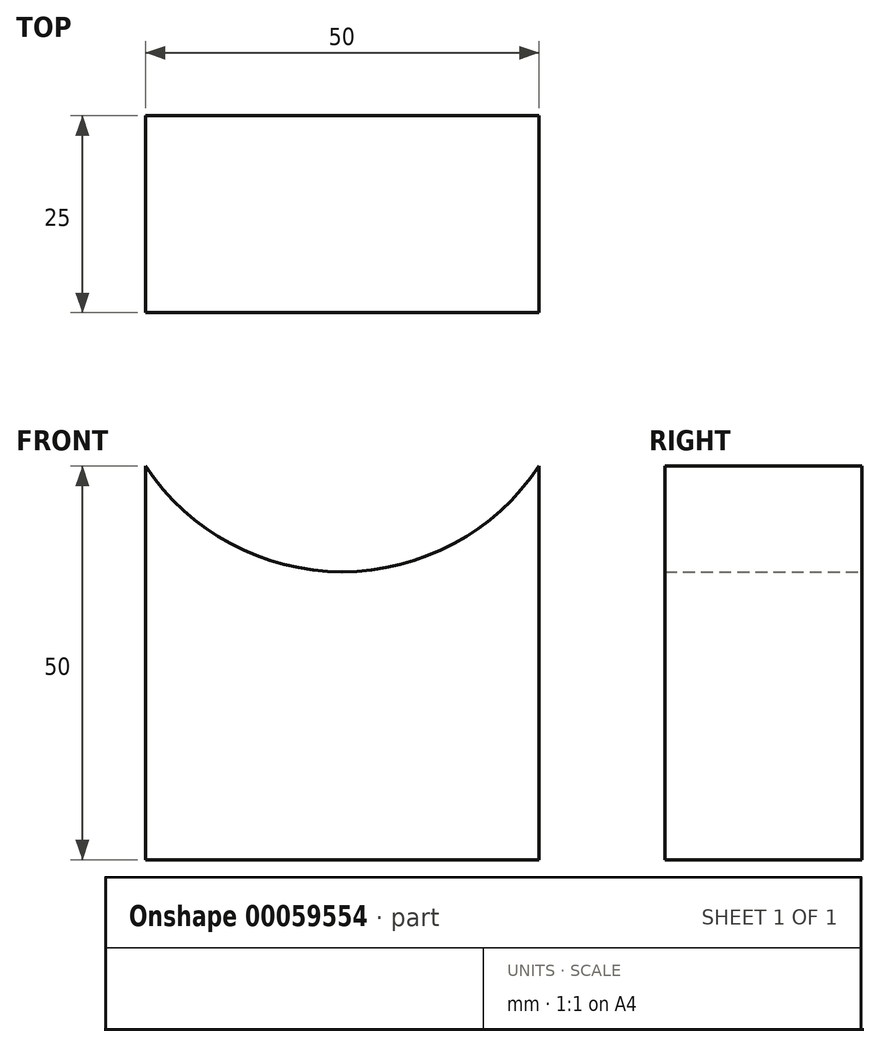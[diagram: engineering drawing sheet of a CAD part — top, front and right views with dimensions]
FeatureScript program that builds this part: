
annotation { "Feature Type Name" : "Feature", "Feature Type Description" : "" }
export const myFeature = defineFeature(function(context is Context, id is Id, definition is map)
    precondition{}
    {
        {
            var Q0;
            Q0=qCreatedBy(makeId("Front.planeOp"),FACE);
            var sketch = newSketch(context, id + "F0", { "sketchPlane" : qUnion([Q0])});
            skLineSegment(sketch, "E0.top", {"start": v(-25, -25) * mm, "end": v(25, -25) * mm});
            skLineSegment(sketch, "E0.left", {"start": v(-25, 25) * mm, "end": v(-25, -25) * mm});
            skLineSegment(sketch, "E0.right", {"start": v(25, 25) * mm, "end": v(25, -25) * mm});
            skPoint(sketch, "E0.middle", {"position": v(0, 0) * mm});
            skArc(sketch, "E1", {"start": v(-25, 25) * mm, "mid": v(0, 11.58) * mm, "end": v(25, 25) * mm});
            skSolve(sketch);
        }
        {
            var Q0;
            Q0 = qSketchRegion(id + "F0", true);
            extrude(context, id + "F1", {"entities" : qUnion([Q0]), "depth" : 25 * mm});
        }
    });
